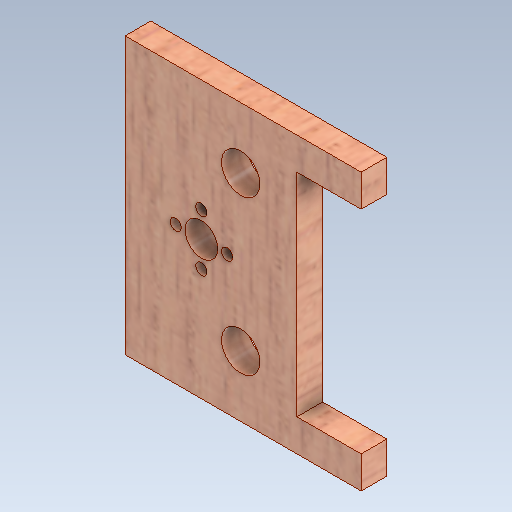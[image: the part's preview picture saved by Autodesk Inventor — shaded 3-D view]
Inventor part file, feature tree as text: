
AUTODESK INVENTOR PART (.ipt)
format: ipt  version: 2020 (Build 240168000, 168)  size: 286,208 bytes
history: native  units: mm
features: extrude x4, sketch x4, other x3, reference x1
ambient origin geometry x8: Origin, YZ Plane, XZ Plane, XY Plane, X Axis, Y Axis, Z Axis, Center Point
bodies: Solid1 (feature_tree)
feature tree (12):
  extrude  "Extrusion1"  Depth=86.0mm
  extrude  "Extrusion4"  Depth=20.0mm
  extrude  "Extrusion5"  Depth=10.0mm TaperAngle=0.0deg
  extrude  "Extrusion6"  Depth=10.0mm TaperAngle=0.0deg
  sketch  "Sketch1"  dims[d0=73.5mm d1=86.0mm]
  sketch  "Sketch4"  dims[d2=8.0mm d3=0.0mm d19=20.0mm]
  sketch  "Sketch5"  dims[d20=66.0mm d21=10.0mm d22=0.0mm]
  reference  "Reference1"
  sketch  "Sketch6"  dims[d23=12.0mm d29=10.0mm d30=0.0mm d37=37.5mm d38=19.0mm d39=19.0mm d40=10.0mm d41=0.0mm d42=3.5mm d43=10.2mm d44=23.751158mm d46=22.0mm d47=16.0mm]
  parser-record x1  (decoder bookkeeping rows leaked as tree rows — omitted from the tree; the rows remain in map.json)
  other  "0005-00-00 Ansamblu_General.iam"
  other  "0005-10-009.ipt:14"
note: 1 file-system path scrubbed to <path> (originals preserved in map.json)
